# Revit family: 90_GM_Urban tree
name_source: partatom
category: Generic Models
units: mm (PartAtom-declared; Revit-internal decimal feet)

## family parameters
Always vertical = Yes
Can host rebar = No
Cut with Voids When Loaded = No
Maintain Annotation Orientation = No
Part Type = Normal
Room Calculation Point = No
Round Connector Dimension = Use Diameter
Shared = No
Work Plane-Based = Yes

## types (4) — shared parameters
Installation = Free modular placement on roof
Irrigation = Via incorporated dripline
zero-valued in all types: Default Elevation

## per-type parameters (varying)
| type | Height | Length | Length with foundation construction | Maximum Windpressure with substructure | Saturated Weight | Tree - 3 meters | Tree - 5 meters | Tree - 6 meters | Tree Height | Weight per m2 | Width | Width with Foundation construction | material_01 | material_02 | material_03 |
| 5 meter tree | 0 mm  [stored 0 ft] | 0 mm  [stored 0 ft] | 0 mm  [stored 0 ft] | 1.50 kN/m² | 1050.00 kg | No | Yes | No |  | 232.00 kg/m² | 0 mm  [stored 0 ft] | 0 mm  [stored 0 ft] |  |  |  |
| 6 meter Tree | 0 mm  [stored 0 ft] | 0 mm  [stored 0 ft] | 0 mm  [stored 0 ft] | 1.50 kN/m² | 1050.00 kg | No | No | Yes |  | 232.00 kg/m² | 0 mm  [stored 0 ft] | 0 mm  [stored 0 ft] |  |  |  |
| 3 meter tree | 800 mm  [stored 2.62467 ft] | 1200 mm  [stored 3.93701 ft] | 2400 mm  [stored 7.87402 ft] | 1.78 kN/m² | 362.00 kg | Yes | No | No | 350cm - 600cm | 251.39 kg/m² | 1200 mm  [stored 3.93701 ft] | 2400 mm  [stored 7.87402 ft] | Powder coated Steel Framing | Jungle mix substrate | Tensions cords |
| No tree | 0 mm  [stored 0 ft] | 0 mm  [stored 0 ft] | 0 mm  [stored 0 ft] | 1.50 kN/m² | 1050.00 kg | No | No | No |  | 232.00 kg/m² | 0 mm  [stored 0 ft] | 0 mm  [stored 0 ft] |  |  |  |

note: [stored X ft] marks values corroborated as IEEE doubles in the binary element streams (Revit-internal decimal feet)

## geometry (parser evidence)
native form markers: Sweep x36
no freeform markers — native parametric forms only
